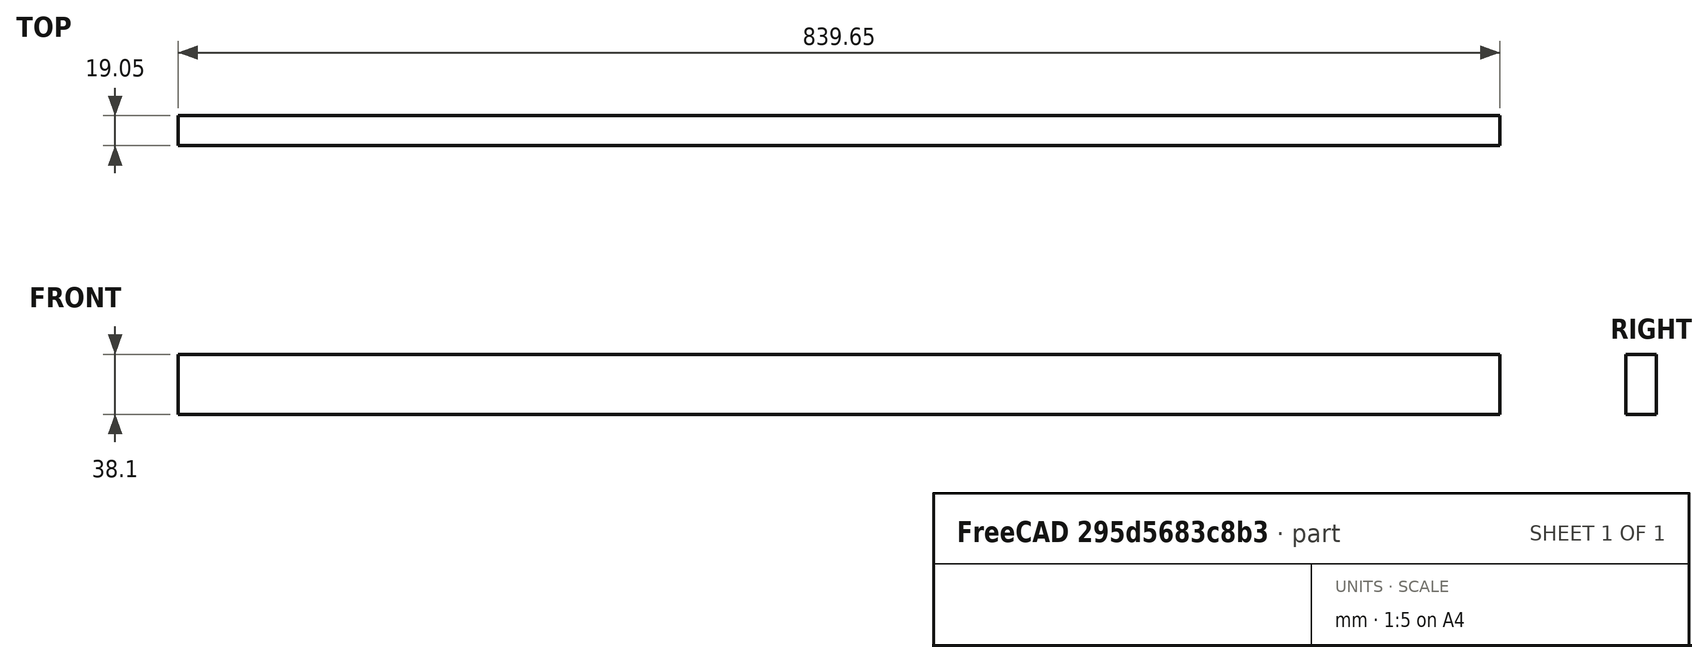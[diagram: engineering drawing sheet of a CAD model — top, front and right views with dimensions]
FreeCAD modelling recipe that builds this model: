
FCSTD DOCUMENT  (FreeCAD 0.20R29177 (Git))
Label: topRightFrontBandStandAlone
License: All rights reserved
LicenseURL: http://en.wikipedia.org/wiki/All_rights_reserved
objects: Sketcher::SketchObject×1, PartDesign::Pad×1, PartDesign::Body×1
note: 4 computed .brp shape members not serialized (recipe doc carries the construction recipe); baked Part::Feature solids carry a one-line shape summary decoded from their .brp

FEATURE [Sketcher::SketchObject] Sketch
  FullyConstrained = true
  MapMode = 5
  Placement = pos=(0,0,0) rot=(1,0,0;1.5708rad)
  Support = -> [XZ_Plane001]
  expr: Constraints[10] = 1.5 * 25.4
  expr: Constraints[9] = 839.65
  sketch-geometry (4):
    g0: LineSegment StartX=0 StartY=0 StartZ=0 EndX=839.65 EndY=0 EndZ=0
    g1: LineSegment StartX=839.65 StartY=0 StartZ=0 EndX=839.65 EndY=38.1 EndZ=0
    g2: LineSegment StartX=839.65 StartY=38.1 StartZ=0 EndX=0 EndY=38.1 EndZ=0
    g3: LineSegment StartX=0 StartY=38.1 StartZ=0 EndX=0 EndY=0 EndZ=0
  constraints (11):
    c: Coincident(g0,g1)
    c: Coincident(g1,g2)
    c: Coincident(g2,g3)
    c: Coincident(g3,g0)
    c: Horizontal(g0)
    c: Horizontal(g2)
    c: Vertical(g1)
    c: Vertical(g3)
    c: Coincident(g0,g-1)
    c: DistanceX(g0,g0) = 839.65
    c: DistanceY(g3,g3) = 38.1
FEATURE [PartDesign::Pad] Pad
  Direction = (0,-1,-2e-16)
  Length = 19.05
  Length2 = 10
  Placement = pos=(0,0,0) rot=(1,0,0;1.5708rad)
  Profile = -> Sketch
  ReferenceAxis = -> Sketch [N_Axis]
  Type = 0
  expr: Length = 3 / 4 * 25.4
FEATURE [PartDesign::Body] Body001
  Group = -> [Sketch,Pad]
  Origin = -> Origin001
  Tip = -> Pad
